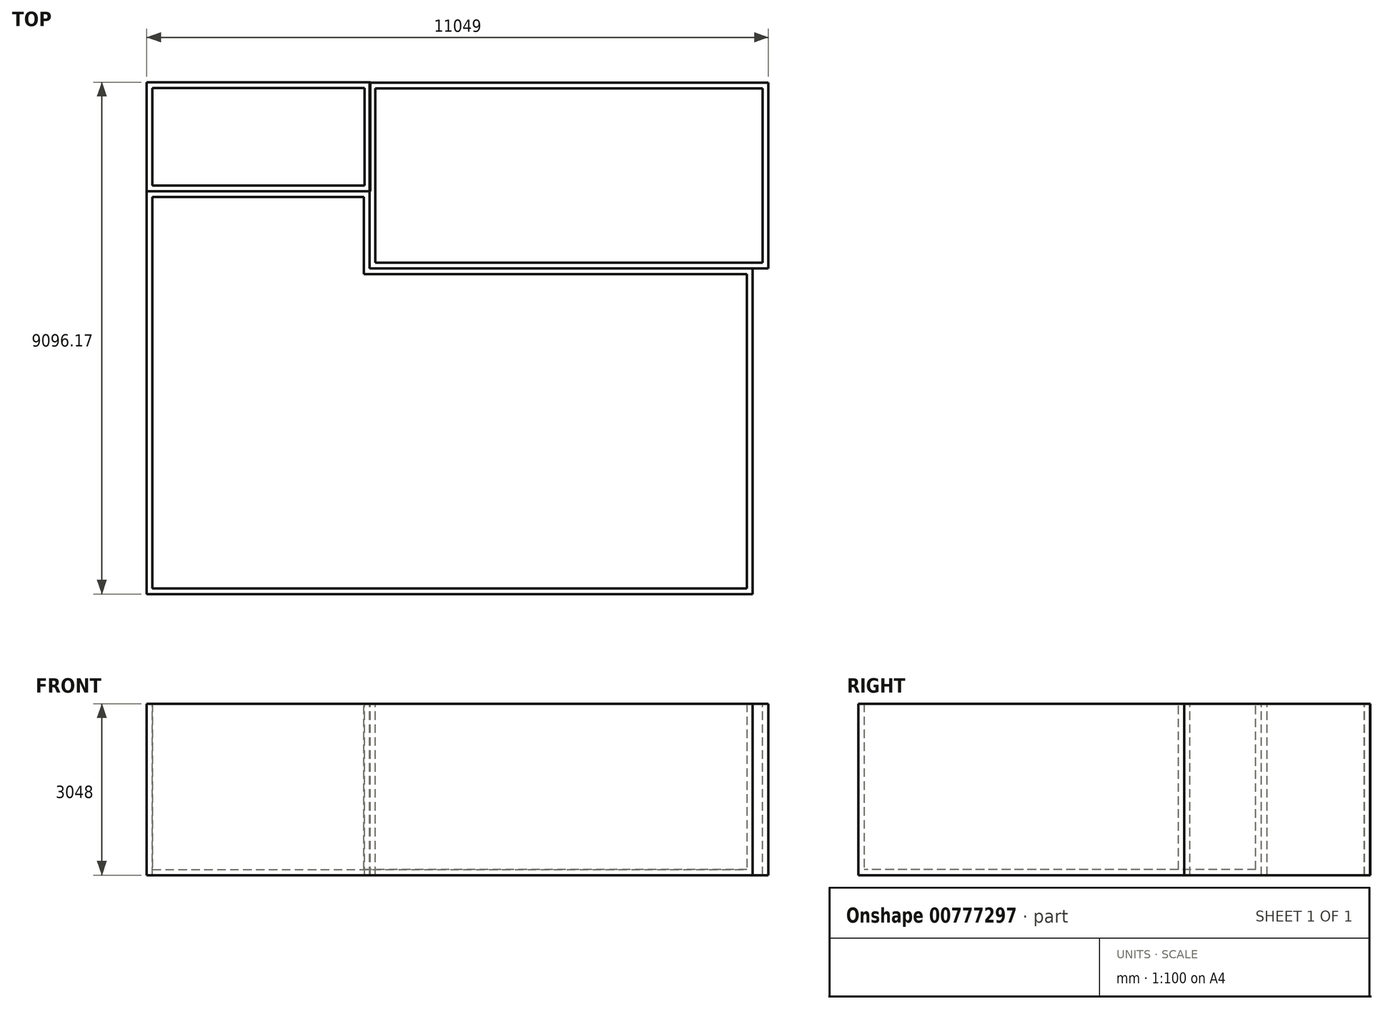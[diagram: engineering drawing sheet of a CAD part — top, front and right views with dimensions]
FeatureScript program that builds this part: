
annotation { "Feature Type Name" : "Feature", "Feature Type Description" : "" }
export const myFeature = defineFeature(function(context is Context, id is Id, definition is map)
    precondition{}
    {
        {
            var Q0;
            Q0=qCreatedBy(makeId("Top.planeOp"),FACE);
            var sketch = newSketch(context, id + "F0", { "sketchPlane" : qUnion([Q0])});
            skLineSegment(sketch, "E0.bottom", {"start": v(-5384.8, 3581.4) * mm, "end": v(5384.8, 3581.4) * mm});
            skLineSegment(sketch, "E0.top", {"start": v(-5384.8, -3581.4) * mm, "end": v(5384.8, -3581.4) * mm});
            skLineSegment(sketch, "E0.left", {"start": v(-5384.8, 3581.4) * mm, "end": v(-5384.8, -3581.4) * mm});
            skLineSegment(sketch, "E0.right", {"start": v(5384.8, 3581.4) * mm, "end": v(5384.8, -3581.4) * mm});
            skSolve(sketch);
        }
        {
            var Q0;
            Q0 = qSketchRegion(id + "F0", true);
            extrude(context, id + "F1", {"entities" : qUnion([Q0]), "depth" : 3048 * mm, "offsetDistance" : 25.4 * mm});
        }
        {
            var Q0;
            Q0=makeQuery(id+"F1.opExtrude","CAP_FACE",FACE,{"disambiguationData":[OSD([sQuery(id+"F0.wireOp",EDGE,"E0.bottom"),sQuery(id+"F0.wireOp",EDGE,"E0.top"),sQuery(id+"F0.wireOp",EDGE,"E0.left"),sQuery(id+"F0.wireOp",EDGE,"E0.right")])],"isStart":false});
            var sketch = newSketch(context, id + "F2", { "sketchPlane" : qUnion([Q0])});
            skLineSegment(sketch, "E1.bottom", {"start": v(5384.8, 3581.4) * mm, "end": v(-1422.4, 3581.4) * mm});
            skLineSegment(sketch, "E1.top", {"start": v(5384.8, 2209.8) * mm, "end": v(-1422.4, 2209.8) * mm});
            skLineSegment(sketch, "E1.left", {"start": v(5384.8, 3581.4) * mm, "end": v(5384.8, 2209.8) * mm});
            skLineSegment(sketch, "E1.right", {"start": v(-1422.4, 3581.4) * mm, "end": v(-1422.4, 2209.8) * mm});
            skSolve(sketch);
        }
        {
            var Q0;
            Q0 = qSketchRegion(id + "F2", true);
            extrude(context, id + "F3", {"entities" : qUnion([Q0]), "operationType" : NewBodyOperationType.REMOVE, "endBound" : BoundingType.THROUGH_ALL, "oppositeDirection" : true, "depth" : 25.4 * mm, "offsetDistance" : 25.4 * mm});
        }
        {
            var Q0;
            Q0=makeQuery(id+"F1.opExtrude","CAP_FACE",FACE,{"disambiguationData":[OSD([sQuery(id+"F0.wireOp",EDGE,"E0.bottom"),sQuery(id+"F0.wireOp",EDGE,"E0.top"),sQuery(id+"F0.wireOp",EDGE,"E0.left"),sQuery(id+"F0.wireOp",EDGE,"E0.right")])],"isStart":false});
            shell(context, id + "F4", {"entities" : qUnion([Q0]), "thickness" : 101.6 * mm});
        }
        {
            var Q0;
            Q0=makeQuery(id+"F1.opExtrude","CAP_FACE",FACE,{"disambiguationData":[OSD([sQuery(id+"F0.wireOp",EDGE,"E0.bottom"),sQuery(id+"F0.wireOp",EDGE,"E0.top"),sQuery(id+"F0.wireOp",EDGE,"E0.left"),sQuery(id+"F0.wireOp",EDGE,"E0.right")])],"isStart":false});
            var sketch = newSketch(context, id + "F5", { "sketchPlane" : qUnion([Q0])});
            skLineSegment(sketch, "E2.bottom", {"start": v(-1422.4, 2209.8) * mm, "end": v(5664.2, 2209.8) * mm});
            skLineSegment(sketch, "E2.top", {"start": v(-1422.4, 5511.8) * mm, "end": v(5664.2, 5511.8) * mm});
            skLineSegment(sketch, "E2.left", {"start": v(-1422.4, 2209.8) * mm, "end": v(-1422.4, 5511.8) * mm});
            skLineSegment(sketch, "E2.right", {"start": v(5664.2, 2209.8) * mm, "end": v(5664.2, 5511.8) * mm});
            skSolve(sketch);
        }
        {
            var Q0;
            {var subQ2=sQuery(id+"F5.wireOp",EDGE,"E2.top");Q0=makeQuery(id+"F5.imprint","IMPRINT",FACE,{"disambiguationData":[TD([[makeQuery(id+"F5.imprint","IMPRINT",EDGE,{"derivedFrom":subQ2}),-1.0]])]});}
            extrude(context, id + "F6", {"entities" : qUnion([Q0]), "oppositeDirection" : true, "depth" : 3048 * mm, "offsetDistance" : 25.4 * mm});
        }
        {
            var Q0;
            Q0=makeQuery(id+"F6.opExtrude","CAP_FACE",FACE,{"disambiguationData":[OSD([sQuery(id+"F5.wireOp",EDGE,"E2.bottom"),sQuery(id+"F5.wireOp",EDGE,"E2.top"),sQuery(id+"F5.wireOp",EDGE,"E2.left"),sQuery(id+"F5.wireOp",EDGE,"E2.right")])],"isStart":true});
            var Q1;
            Q1=makeQuery(id+"F6.opExtrude","CAP_FACE",FACE,{"disambiguationData":[OSD([sQuery(id+"F5.wireOp",EDGE,"E2.bottom"),sQuery(id+"F5.wireOp",EDGE,"E2.top"),sQuery(id+"F5.wireOp",EDGE,"E2.left"),sQuery(id+"F5.wireOp",EDGE,"E2.right")])],"isStart":false});
            shell(context, id + "F7", {"entities" : qUnion([Q0, Q1]), "thickness" : 101.6 * mm});
        }
        {
            var Q0;
            Q0=makeQuery(id+"F1.opExtrude","CAP_FACE",FACE,{"disambiguationData":[OSD([sQuery(id+"F0.wireOp",EDGE,"E0.bottom"),sQuery(id+"F0.wireOp",EDGE,"E0.top"),sQuery(id+"F0.wireOp",EDGE,"E0.left"),sQuery(id+"F0.wireOp",EDGE,"E0.right")])],"isStart":false});
            var sketch = newSketch(context, id + "F8", { "sketchPlane" : qUnion([Q0])});
            skLineSegment(sketch, "E3.bottom", {"start": v(-5384.8, 3581.4) * mm, "end": v(-1415.31, 3581.4) * mm});
            skLineSegment(sketch, "E3.top", {"start": v(-5384.8, 5514.77) * mm, "end": v(-1415.31, 5514.77) * mm});
            skLineSegment(sketch, "E3.left", {"start": v(-5384.8, 3581.4) * mm, "end": v(-5384.8, 5514.77) * mm});
            skLineSegment(sketch, "E3.right", {"start": v(-1415.31, 3581.4) * mm, "end": v(-1415.31, 5514.77) * mm});
            skSolve(sketch);
        }
        {
            var Q0;
            Q0 = qSketchRegion(id + "F8", true);
            extrude(context, id + "F9", {"entities" : qUnion([Q0]), "oppositeDirection" : true, "depth" : 3048 * mm, "offsetDistance" : 25.4 * mm});
        }
        {
            var Q0;
            Q0=makeQuery(id+"F9.opExtrude","CAP_FACE",FACE,{"disambiguationData":[OSD([sQuery(id+"F8.wireOp",EDGE,"E3.bottom"),sQuery(id+"F8.wireOp",EDGE,"E3.top"),sQuery(id+"F8.wireOp",EDGE,"E3.left"),sQuery(id+"F8.wireOp",EDGE,"E3.right")])],"isStart":false});
            var Q1;
            Q1=makeQuery(id+"F9.opExtrude","CAP_FACE",FACE,{"disambiguationData":[OSD([sQuery(id+"F8.wireOp",EDGE,"E3.bottom"),sQuery(id+"F8.wireOp",EDGE,"E3.top"),sQuery(id+"F8.wireOp",EDGE,"E3.left"),sQuery(id+"F8.wireOp",EDGE,"E3.right")])],"isStart":true});
            shell(context, id + "F10", {"entities" : qUnion([Q0, Q1]), "thickness" : 101.6 * mm});
        }
    });
